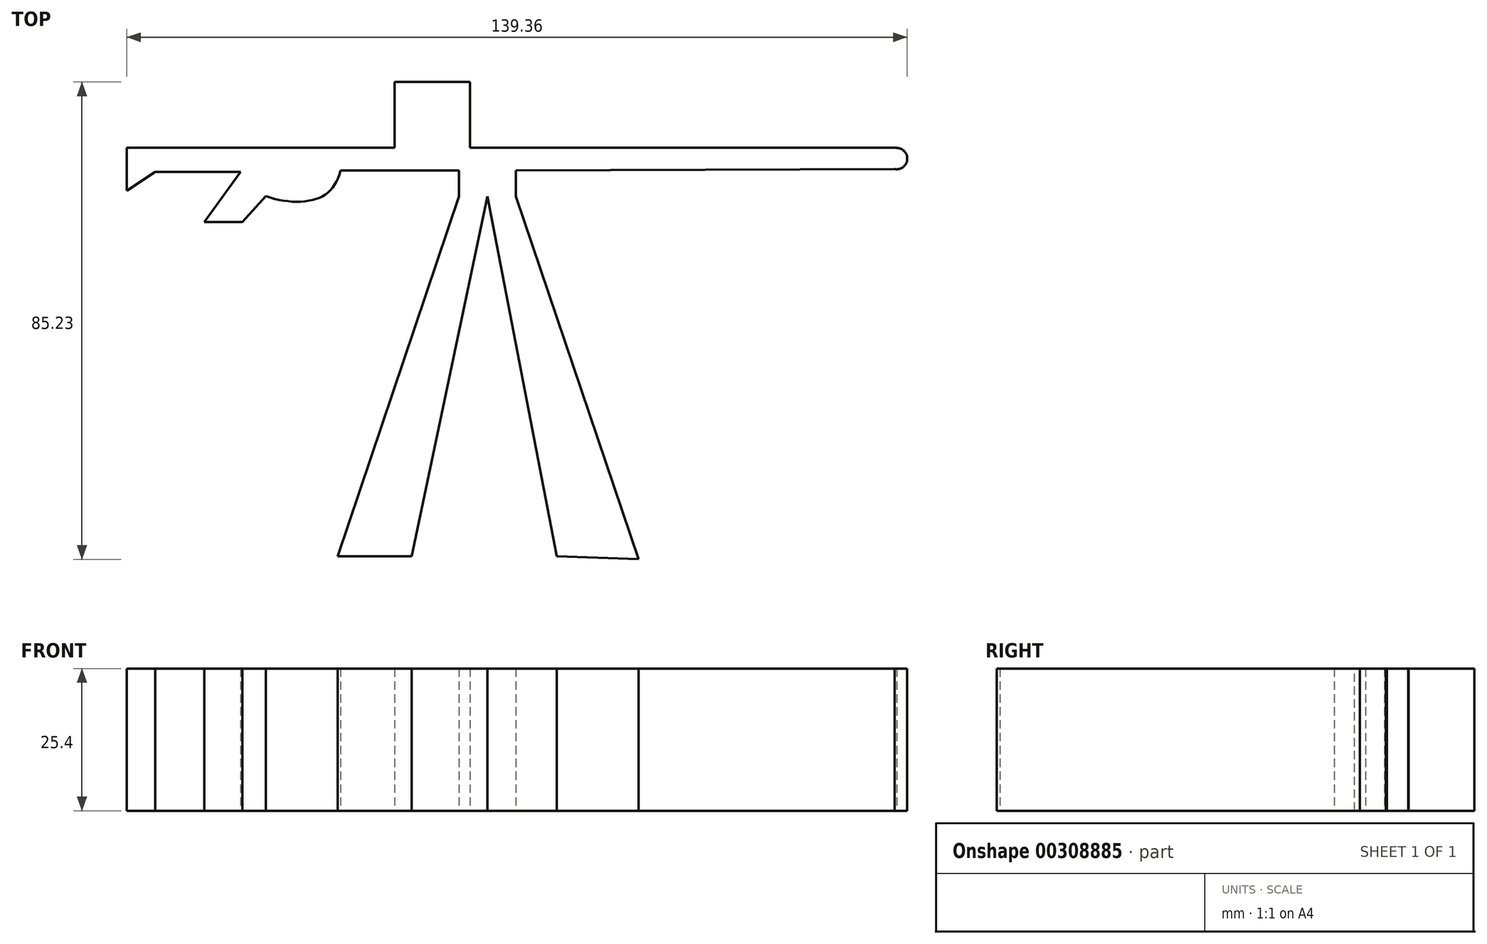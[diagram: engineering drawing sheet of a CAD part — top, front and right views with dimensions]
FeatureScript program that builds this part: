
annotation { "Feature Type Name" : "Feature", "Feature Type Description" : "" }
export const myFeature = defineFeature(function(context is Context, id is Id, definition is map)
    precondition{}
    {
        {
            var Q0;
            Q0=qCreatedBy(makeId("Top.planeOp"),FACE);
            var sketch = newSketch(context, id + "F0", { "sketchPlane" : qUnion([Q0])});
            skLineSegment(sketch, "E0.bottom", {"start": v(-21.65, 40.09) * mm, "end": v(-8.16, 40.09) * mm});
            skLineSegment(sketch, "E0.left", {"start": v(-21.65, 40.09) * mm, "end": v(-21.65, 33.37) * mm});
            skLineSegment(sketch, "E0.right", {"start": v(-8.16, 40.09) * mm, "end": v(-8.16, 33.37) * mm});
            skLineSegment(sketch, "E1", {"start": v(-21.65, 33.37) * mm, "end": v(-21.65, 28.35) * mm});
            skLineSegment(sketch, "E2", {"start": v(-8.16, 33.37) * mm, "end": v(-8.16, 28.35) * mm});
            skLineSegment(sketch, "E3", {"start": v(-46.07, 28.35) * mm, "end": v(-8.16, 28.35) * mm});
            skLineSegment(sketch, "E4", {"start": v(-40.44, 24.33) * mm, "end": v(-48.8, 15.1) * mm});
            skLineSegment(sketch, "E5", {"start": v(-48.8, 15.1) * mm, "end": v(-55.58, 15.1) * mm});
            skLineSegment(sketch, "E6", {"start": v(-55.58, 15.1) * mm, "end": v(-46.07, 28.35) * mm});
            skFitSpline(sketch, "E7", {"points": [v(-31.27, 24.33) * mm, v(-35.32, 19.3) * mm, v(-44.61, 19.71) * mm], "startDerivative": vector(-4.8, -17.54) * mm, "endDerivative": vector(-17.26, 6.3) * mm});
            skFitSpline(sketch, "E8", {"points": [v(-37.53, 24.33) * mm, v(-35.93, 21.63) * mm, v(-41.9, 22.7) * mm], "startDerivative": vector(4.92, -12.76) * mm, "endDerivative": vector(-20.89, 7.02) * mm});
            skLineSegment(sketch, "E9", {"start": v(-46.07, 28.35) * mm, "end": v(-69.46, 28.35) * mm});
            skLineSegment(sketch, "E10", {"start": v(-69.46, 28.35) * mm, "end": v(-69.46, 20.67) * mm});
            skLineSegment(sketch, "E11", {"start": v(-69.46, 20.67) * mm, "end": v(-64.4, 24.05) * mm});
            skLineSegment(sketch, "E12", {"start": v(-64.4, 24.05) * mm, "end": v(-49.16, 24.05) * mm});
            skLineSegment(sketch, "E13", {"start": v(-10.16, 24.33) * mm, "end": v(-10.16, 19.69) * mm});
            skLineSegment(sketch, "E14", {"start": v(0, 19.69) * mm, "end": v(0, 24.33) * mm});
            skLineSegment(sketch, "E15", {"start": v(-10.16, 19.69) * mm, "end": v(-31.78, -44.57) * mm});
            skLineSegment(sketch, "E16", {"start": v(-31.78, -44.57) * mm, "end": v(-18.56, -44.57) * mm});
            skLineSegment(sketch, "E17", {"start": v(-18.56, -44.57) * mm, "end": v(-5.08, 19.69) * mm});
            skLineSegment(sketch, "E18", {"start": v(-5.08, 19.69) * mm, "end": v(7.31, -44.57) * mm});
            skLineSegment(sketch, "E19", {"start": v(0, 19.69) * mm, "end": v(21.94, -45.14) * mm});
            skLineSegment(sketch, "E20", {"start": v(21.94, -45.14) * mm, "end": v(7.31, -44.57) * mm});
            skLineSegment(sketch, "E21", {"start": v(-21.65, 33.37) * mm, "end": v(-8.16, 33.37) * mm});
            skLineSegment(sketch, "E22.trimOffspring", {"start": v(-10.16, 24.33) * mm, "end": v(-40.44, 24.33) * mm});
            skLineSegment(sketch, "E23", {"start": v(-10.16, 19.69) * mm, "end": v(0, 19.69) * mm});
            skLineSegment(sketch, "E24", {"start": v(-10.16, 24.33) * mm, "end": v(0, 24.33) * mm});
            skLineSegment(sketch, "E25", {"start": v(-8.16, 28.35) * mm, "end": v(68.04, 28.35) * mm});
            skLineSegment(sketch, "E26", {"start": v(68.04, 24.54) * mm, "end": v(0, 24.33) * mm});
            skCircle(sketch, "E27", {"center": v(68, 26.42) * mm, "radius": 1.9 * mm});
            skLineSegment(sketch, "E28", {"start": v(68.04, 24.54) * mm, "end": v(68.04, 24.51) * mm});
            skLineSegment(sketch, "E29", {"start": v(68.04, 28.35) * mm, "end": v(68.05, 28.32) * mm});
            skSolve(sketch);
        }
        {
            var Q0;
            Q0=makeQuery(id+"F0.imprint","IMPRINT",FACE,{"disambiguationData":[TD([[makeQuery(id+"F0.imprint","IMPRINT",EDGE,{"derivedFrom":sQuery(id+"F0.wireOp",EDGE,"E0.bottom")}),-1.0]])]});
            var Q1;
            {var subQ0=sQuery(id+"F0.wireOp",EDGE,"E9");Q1=makeQuery(id+"F0.imprint","IMPRINT",FACE,{"disambiguationData":[TD([[makeQuery(id+"F0.imprint","IMPRINT",EDGE,{"derivedFrom":subQ0}),1.0]])]});}
            var Q2;
            {var subQ0=sQuery(id+"F0.wireOp",EDGE,"E15");Q2=makeQuery(id+"F0.imprint","IMPRINT",FACE,{"disambiguationData":[TD([[makeQuery(id+"F0.imprint","IMPRINT",EDGE,{"derivedFrom":subQ0}),1.0]])]});}
            var Q3;
            {var subQ0=sQuery(id+"F0.wireOp",EDGE,"E18");Q3=makeQuery(id+"F0.imprint","IMPRINT",FACE,{"disambiguationData":[TD([[makeQuery(id+"F0.imprint","IMPRINT",EDGE,{"derivedFrom":subQ0}),1.0]])]});}
            var Q4;
            {var subQ0=sQuery(id+"F0.wireOp",EDGE,"E1");Q4=makeQuery(id+"F0.imprint","IMPRINT",FACE,{"disambiguationData":[TD([[makeQuery(id+"F0.imprint","IMPRINT",EDGE,{"derivedFrom":subQ0}),1.0]])]});}
            var Q5;
            {var subQ0=sQuery(id+"F0.wireOp",EDGE,"E7");Q5=makeQuery(id+"F0.imprint","IMPRINT",FACE,{"disambiguationData":[TD([[makeQuery(id+"F0.imprint","IMPRINT",EDGE,{"derivedFrom":subQ0}),-1.0]])]});}
            var Q6;
            {var subQ3=sQuery(id+"F0.wireOp",EDGE,"E13");Q6=makeQuery(id+"F0.imprint","IMPRINT",FACE,{"disambiguationData":[TD([[makeQuery(id+"F0.imprint","IMPRINT",EDGE,{"derivedFrom":subQ3}),1.0]])]});}
            var Q7;
            {var subQ4=sQuery(id+"F0.wireOp",EDGE,"E5");Q7=makeQuery(id+"F0.imprint","IMPRINT",FACE,{"disambiguationData":[TD([[makeQuery(id+"F0.imprint","IMPRINT",EDGE,{"derivedFrom":subQ4}),-1.0]])]});}
            var Q8;
            {var subQ3=sQuery(id+"F0.wireOp",EDGE,"E8");Q8=makeQuery(id+"F0.imprint","IMPRINT",FACE,{"disambiguationData":[TD([[makeQuery(id+"F0.imprint","IMPRINT",EDGE,{"derivedFrom":subQ3}),-1.0]])]});}
            var Q9;
            {var subQ0=sQuery(id+"F0.wireOp",EDGE,"E28");Q9=makeQuery(id+"F0.imprint","IMPRINT",FACE,{"disambiguationData":[TD([[makeQuery(id+"F0.imprint","IMPRINT",EDGE,{"derivedFrom":subQ0}),1.0]])]});}
            var Q10;
            {var subQ0=sQuery(id+"F0.wireOp",EDGE,"E28");Q10=makeQuery(id+"F0.imprint","IMPRINT",FACE,{"disambiguationData":[TD([[makeQuery(id+"F0.imprint","IMPRINT",EDGE,{"derivedFrom":subQ0}),-1.0]])]});}
            extrude(context, id + "F1", {"entities" : qUnion([Q0, Q1, Q2, Q3, Q4, Q5, Q6, Q7, Q8, Q9, Q10]), "depth" : 25.4 * mm});
        }
    });
